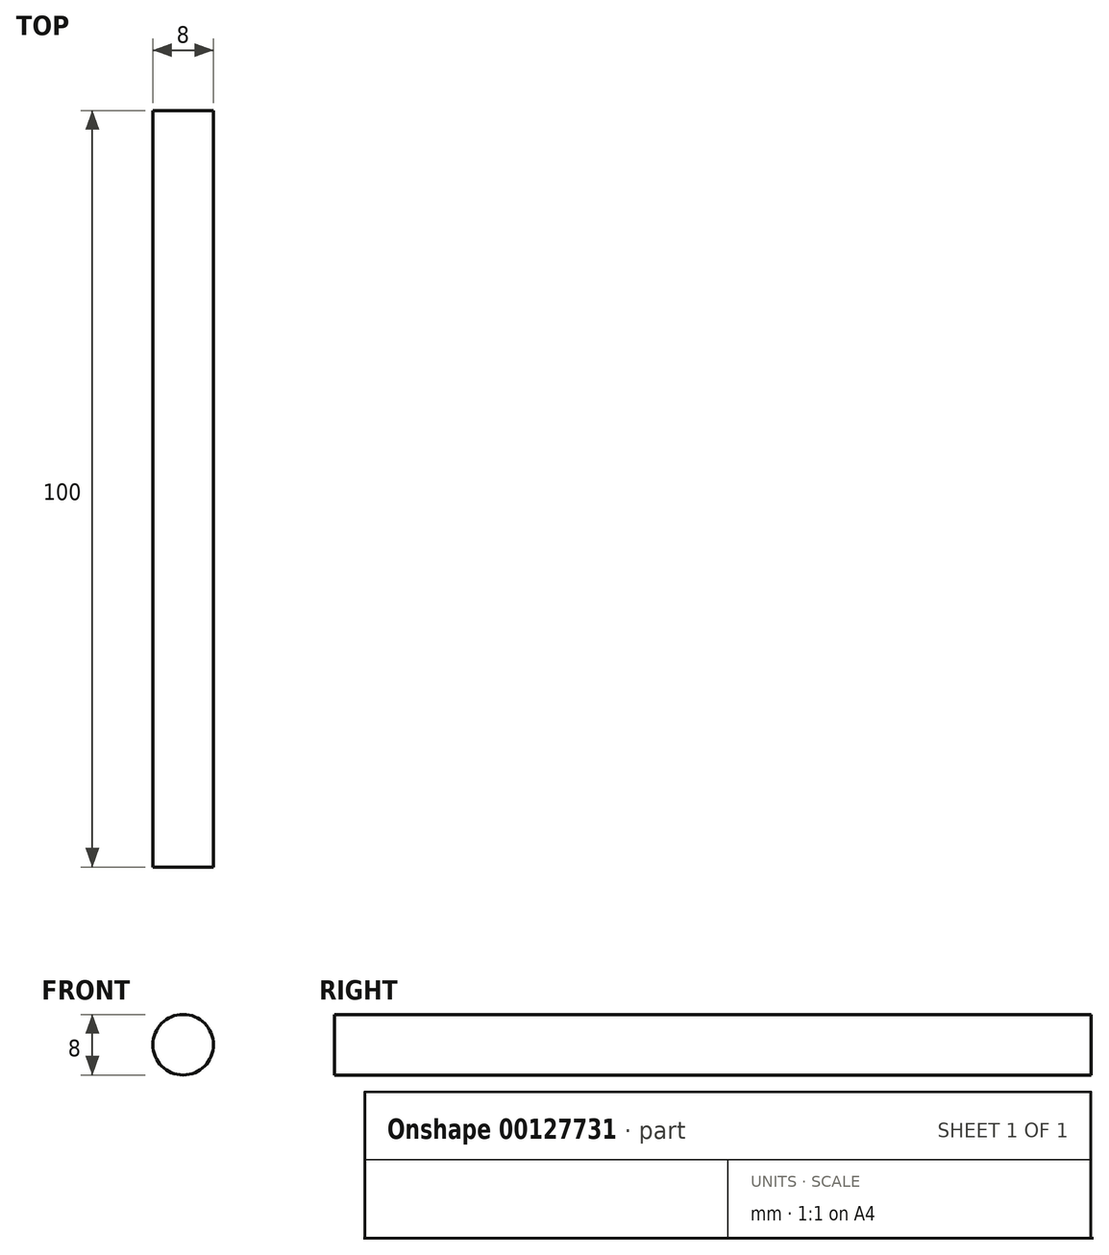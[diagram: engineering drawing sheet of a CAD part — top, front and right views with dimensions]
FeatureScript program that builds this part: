
annotation { "Feature Type Name" : "Feature", "Feature Type Description" : "" }
export const myFeature = defineFeature(function(context is Context, id is Id, definition is map)
    precondition{}
    {
        {
            var Q0;
            Q0=qCreatedBy(makeId("Front.planeOp"),FACE);
            var sketch = newSketch(context, id + "F0", { "sketchPlane" : qUnion([Q0])});
            skCircle(sketch, "E0", {"center": v(0, 0) * mm, "radius": 4 * mm});
            skSolve(sketch);
        }
        {
            var Q0;
            Q0 = qSketchRegion(id + "F0", true);
            extrude(context, id + "F1", {"entities" : qUnion([Q0]), "depth" : 50 * mm, "hasSecondDirection" : true, "secondDirectionOppositeDirection" : true, "secondDirectionDepth" : 50 * mm});
        }
    });
